# Revit family: PAV_ARICA
name_source: partatom
category: Equipement de génie climatique
revit_build: Autodesk Revit 2018 (Build: 20170223_1515(x64)
units: mm (PartAtom-declared; Revit-internal decimal feet)

## family parameters
Basée sur le plan de construction = Non
Classification = Aucun
Cote de connecteur circulaire = Utiliser le diamètre
Couper avec des vides une fois chargée = Non
Partagée = Non
Point de calcul de pièce = Non
Toujours verticalement = Oui
Type d'élément = Normal

## types (3) — shared parameters
BRANCHEMENT_TERRE = Oui
COS_PHI = 0.9
DESCR_ALIM_X = Alimentation électrique, 4G1.5mm²
DOUBLE_ALIMENTATION = Oui
LARG.ASPI = 35 mm  [stored 0.114829 ft]
LARG.BOITE ELECT = 128.5 mm
NBR_POLES = 3
PUISS_APPARENTE_2 = 0 VA
PUISS_ELECT = 1 kW
PUISS_ELECT_2 = 0 kW
TENSION_ALIM = 400 V
Type_coffret = tableau éléctrique EPT : Coffret_PM2_3xSL150R
Zone de maintenance 1 = Oui
Zone de maintenance coffret = Oui

## per-type parameters (varying)
- 17V: DEBIT_ASPI_VIDE=16.0 m³/h; DEBIT_REFOUL_VIDE=16.0 m³/h; DESCR_ASPI=Aspiration Vide; 16m3/h; G1/2"FEM; DESCR_REFOUL=Refoulement Vide; 16m3/h; G1/2"FEM; DIAM_ASPI_VIDE=15 mm  [stored 0.0492126 ft]; DIAM_REFOUL_VIDE=15 mm  [stored 0.0492126 ft]; HAUT.ASPI=193 mm; HAUT.ASPI.VIDE=193 mm; HAUT.POMPE.ENV=205 mm  [stored 0.672572 ft]; HAUT.POMPE.ENV 1=205 mm  [stored 0.672572 ft]; LARG.POMPE.ENV=102.5 mm  [stored 0.336286 ft]; LARG.POMPE.ENV 1=102.5 mm  [stored 0.336286 ft]; LARG.POMPE.ENV 3=68.2 mm; LARG.POMPE.SOCLE (1)=77.5 mm; LARG.POMPE.SOCLE (2)=77.5 mm; LONG.ASPI=110 mm  [stored 0.360892 ft]; LONG.ASPI.VIDE=276.5 mm  [stored 0.907152 ft]; LONG.BOITE.ELECT=104 mm; LONG.BOITE.ELECT.CAB=141.5 mm; LONG.POMPE.ENV (1)=416 mm; LONG.POMPE.ENV (2)=410.2 mm; LONG.POMPE.ENV (3)=452 mm; LONG.POMPE.ENV (4)=342 mm  [stored 1.12205 ft]; LONG.POMPE.ENV (5)=342 mm  [stored 1.12205 ft]; LONG.POMPE.ENV (6)=342 mm  [stored 1.12205 ft]; LONG.POMPE.REG=416 mm; LONG.POMPE.SOCLE (1)=53 mm; LONG.POMPE.SOCLE (2)=242 mm  [stored 0.793963 ft]; LONG.REFOUL=232 mm  [stored 0.761155 ft]; LONG.TROU.BOITE.ELECT=101.5 mm; NEUTRE=Non; NIVEAU_SONORE(dB(A))=61; POIDS(Kg)=22.5 mm  [stored 0.0738189 ft]; PUISS_APPARENTE=611 VA
- 41V: DEBIT_ASPI_VIDE=40.0 m³/h; DEBIT_REFOUL_VIDE=40.0 m³/h; DESCR_ASPI=Aspiration Vide; 40m3/h; G3/4"FEM; DESCR_REFOUL=Refoulement Vide; 40m3/h; G3/4"FEM; DIAM_ASPI_VIDE=20 mm  [stored 0.0656168 ft]; DIAM_REFOUL_VIDE=20 mm  [stored 0.0656168 ft]; HAUT.ASPI=238 mm  [stored 0.78084 ft]; HAUT.ASPI.VIDE=238 mm  [stored 0.78084 ft]; HAUT.POMPE.ENV=250 mm  [stored 0.82021 ft]; HAUT.POMPE.ENV 1=250 mm  [stored 0.82021 ft]; LARG.POMPE.ENV=125 mm  [stored 0.410105 ft]; LARG.POMPE.ENV 1=125 mm  [stored 0.410105 ft]; LARG.POMPE.ENV 3=90.7 mm  [stored 0.297572 ft]; LARG.POMPE.SOCLE (1)=119 mm  [stored 0.39042 ft]; LARG.POMPE.SOCLE (2)=119 mm  [stored 0.39042 ft]; LONG.ASPI=182 mm  [stored 0.597113 ft]; LONG.ASPI.VIDE=348.5 mm  [stored 1.14337 ft]; LONG.BOITE.ELECT=144.5 mm  [stored 0.474081 ft]; LONG.BOITE.ELECT.CAB=182 mm  [stored 0.597113 ft]; LONG.POMPE.ENV (1)=532 mm; LONG.POMPE.ENV (2)=500.2 mm; LONG.POMPE.ENV (3)=572 mm; LONG.POMPE.ENV (4)=432 mm; LONG.POMPE.ENV (5)=432 mm; LONG.POMPE.ENV (6)=432 mm; LONG.POMPE.REG=532 mm; LONG.POMPE.SOCLE (1)=111 mm; LONG.POMPE.SOCLE (2)=260 mm  [stored 0.853018 ft]; LONG.REFOUL=352 mm  [stored 1.15486 ft]; LONG.TROU.BOITE.ELECT=142 mm  [stored 0.465879 ft]; NEUTRE=Oui; NIVEAU_SONORE(dB(A))=67; POIDS(Kg)=38 mm  [stored 0.124672 ft]; PUISS_APPARENTE=1389 VA
- 27V: DEBIT_ASPI_VIDE=25.0 m³/h; DEBIT_REFOUL_VIDE=25.0 m³/h; DESCR_ASPI=Aspiration Vide; 25m3/h; G3/4"FEM; DESCR_REFOUL=Refoulement Vide; 25m3/h; G3/4"FEM; DIAM_ASPI_VIDE=20 mm  [stored 0.0656168 ft]; DIAM_REFOUL_VIDE=20 mm  [stored 0.0656168 ft]; HAUT.ASPI=238 mm  [stored 0.78084 ft]; HAUT.ASPI.VIDE=238 mm  [stored 0.78084 ft]; HAUT.POMPE.ENV=250 mm  [stored 0.82021 ft]; HAUT.POMPE.ENV 1=250 mm  [stored 0.82021 ft]; LARG.POMPE.ENV=125 mm  [stored 0.410105 ft]; LARG.POMPE.ENV 1=125 mm  [stored 0.410105 ft]; LARG.POMPE.ENV 3=90.7 mm  [stored 0.297572 ft]; LARG.POMPE.SOCLE (1)=119 mm  [stored 0.39042 ft]; LARG.POMPE.SOCLE (2)=119 mm  [stored 0.39042 ft]; LONG.ASPI=120.5 mm  [stored 0.395341 ft]; LONG.ASPI.VIDE=286.5 mm  [stored 0.939961 ft]; LONG.BOITE.ELECT=125.5 mm; LONG.BOITE.ELECT.CAB=163 mm  [stored 0.534777 ft]; LONG.POMPE.ENV (1)=465 mm; LONG.POMPE.ENV (2)=455.2 mm; LONG.POMPE.ENV (3)=505 mm; LONG.POMPE.ENV (4)=364.5 mm; LONG.POMPE.ENV (5)=364.5 mm; LONG.POMPE.ENV (6)=364.5 mm; LONG.POMPE.REG=465 mm; LONG.POMPE.SOCLE (1)=76 mm  [stored 0.249344 ft]; LONG.POMPE.SOCLE (2)=260 mm  [stored 0.853018 ft]; LONG.REFOUL=281 mm  [stored 0.921916 ft]; LONG.TROU.BOITE.ELECT=123 mm  [stored 0.403543 ft]; NEUTRE=Oui; NIVEAU_SONORE(dB(A))=62; POIDS(Kg)=26 mm; PUISS_APPARENTE=833 VA

note: [stored X ft] marks values corroborated as IEEE doubles in the binary element streams (Revit-internal decimal feet)
